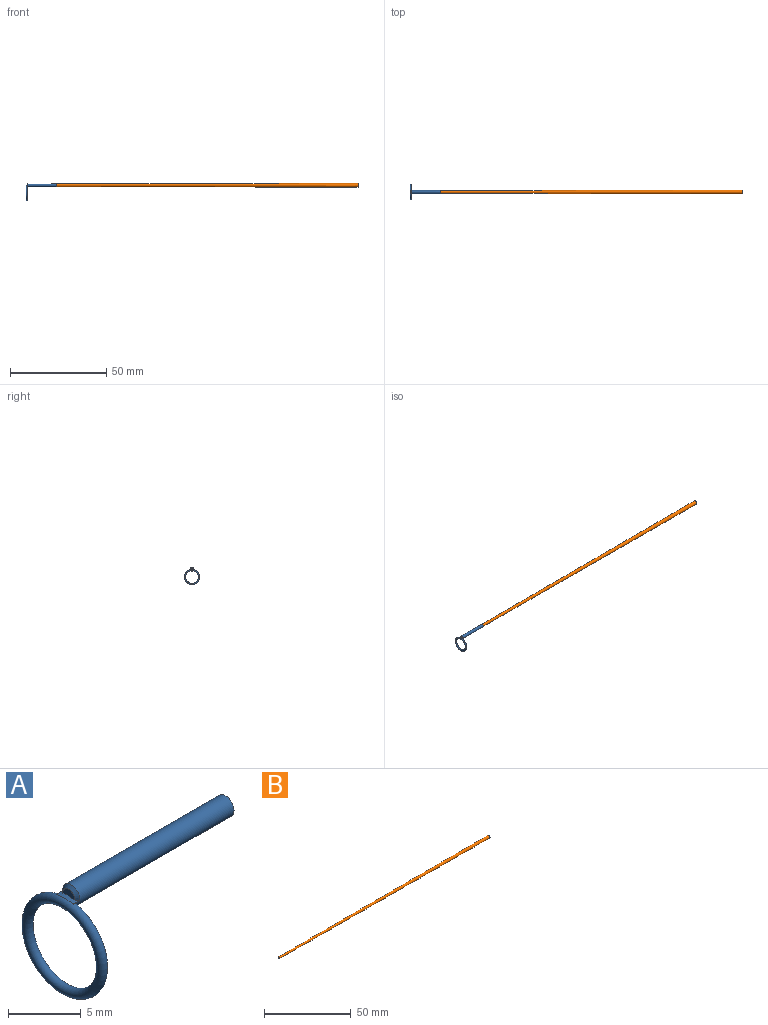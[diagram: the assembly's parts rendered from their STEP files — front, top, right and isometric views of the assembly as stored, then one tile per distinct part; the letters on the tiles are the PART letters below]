
ASSEMBLY  parts=2 mates=1
PART A: 10 faces, bbox 16x8.7x9.2 mm
  f0: plane 0.57x0.06mm, normal (-1,0,0), area 0mm2, adj f4,f7
  f1: plane 1.27x1.27mm, normal (1,0,0), area 1.3mm2, adj f2
  f2: cylinder r=0.64mm len=15.05mm, axis (1,0,0), area 60mm2, adj f1,f3
  f3: plane 1.65x1.65mm, normal (1,0,0), area 0.9mm2, adj f2,f4
  f4: cylinder r=0.83mm len=15.62mm, axis (1,0,0), area 78.5mm2, adj f0,f3,f6,f7,f8,f9
  f5: plane 1.14x0.61mm, normal (-1,0,0), area 0.5mm2, adj f6,f9
  f6: cylinder r=4mm len=1.64mm, axis (1,0,0), area 0.7mm2, adj f4,f5,f8,f9
  f7: cylinder r=3.24mm len=0.57mm, axis (1,0,0), area 0.2mm2, adj f0,f4,f8
  f8: torus R=3.62mm, axis (-1,0,0), area 52.9mm2, adj f4,f6,f7
  f9: cone r=0.83mm half-angle=45deg, axis (1,0,0), area 0.8mm2, adj f4,f5,f6
PART B: 3 faces, bbox 171.5x2x2 mm
  f0: plane 2.03x2.03mm, normal (1,0,0), area 3.2mm2, adj f1
  f1: cone r=0.64mm half-angle=0.1deg, axis (1,0,0), area 889.3mm2, adj f0,f2
  f2: plane 1.27x1.27mm, normal (-1,0,0), area 1.3mm2, adj f1
PLACE A t=(-70.68,0,0)mm
PLACE B t=(85.72,0,0)mm
MATE fastened A.f2 <-> B.f1  axis (1,0,0) through (-85.72,0,0)mm
